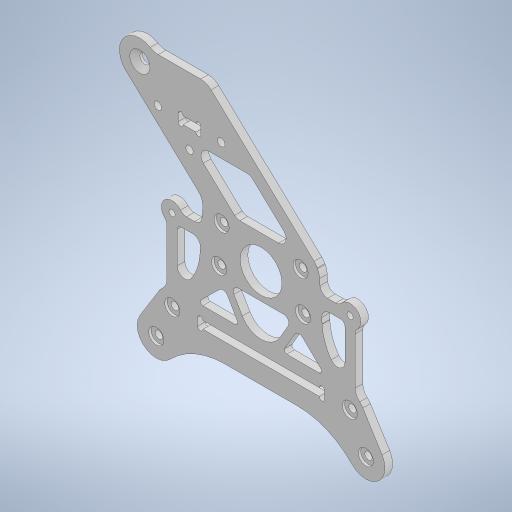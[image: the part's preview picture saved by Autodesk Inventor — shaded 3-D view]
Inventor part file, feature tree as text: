
AUTODESK INVENTOR PART (.ipt)
format: ipt  version: 2023.1 (Build 271208000, 208)  size: 505,856 bytes
history: native  units: mm
features: extrude x3, other x1, chamfer x1, sketch x1
ambient origin geometry x8: Origin, YZ Plane, XZ Plane, XY Plane, X Axis, Y Axis, Z Axis, Center Point
bodies: Body1 (feature_tree)
feature tree (6):
  other  "ソリッド1"
  extrude  "押し出し1"  Depth=3.0mm TaperAngle=0.0deg
  extrude  "押し出し2"  Depth=2.0mm TaperAngle=0.0deg
  extrude  "押し出し3"  Depth=3.0mm TaperAngle=0.0deg
  chamfer  "面取り1"  Distance=3.5mm
  sketch  "スケッチ2"
